# Revit family: Faucet_Kitchen-Two_Handle-American_Standard-Monterrey-6540.188
name_source: partatom
category: Plumbing Fixtures
revit_build: Autodesk Revit 2018 (Build: 20170223_1515(x64)
units: mm (PartAtom-declared; Revit-internal decimal feet)

## family parameters
Always vertical = No
Cut with Voids When Loaded = No
OmniClass Number = 23.45.55.17
OmniClass Title = Mixing Faucets
Part Type = Normal
Room Calculation Point = No
Round Connector Dimension = Use Diameter
Shared = Yes
Work Plane-Based = Yes

## types (1)
- 6540.188.002
    ADA Compliant = Yes
    Assembly Code = D2020300
    CW Connection = Yes
    CWFU = 1.5
    Default Elevation = 0"
    Description = Monterrey Two-Handle Widespread Lavatory Faucet With Laminar Flow In Base Of Spout Rigid/Swivel Gooseneck Spout With 8" Reach.
    Finish = Brass-American_Standard-002-Polished_Chrome
    Flow Rate = 1.5 gpm/5.7L/min
    HW Connection = Yes
    HWFU = 1.5
    Handle Length = 3 7/8"
    Height = 12 1/2"
    IAPMO Compliance = "Product meets or exceeds: ANSI A117.1, ASME A112.18.1, CSA B125.1, NSF 372"
    Installation Type = Deck Mounted
    Length = 15 3/4"
    Manufacturer = American Standard
    Material = Brass-American_Standard-002-Polished_Chrome
    Model = 6540.188.002
    Price = Prices may vary. Please consult Manufacturer Representative for most up-to-date price list.
    Product Documentation Link = https://www.americanstandard-us.com
    Product Page URL = https://www.americanstandard-us.com
    Revised Date = 12/05/2016
    Specification = 1.5 gpm Pressure Compensating Laminar Flow device in base of spout. Plain spout end. Field-Convertible rigid/swivel gooseneck spout with 8" reach. Vandal-Resistant Wrist Blade Handles. Less drain and pop-up hole.
    URL = http://www.americanstandard-us.com
    Vent Connection = No
    WFU = 0
    Warranty Information = 5 Year limited
    Waste Connection = No
    Width = 8"

## geometry (parser evidence)
native form markers: Sweep x2
no freeform markers — native parametric forms only
